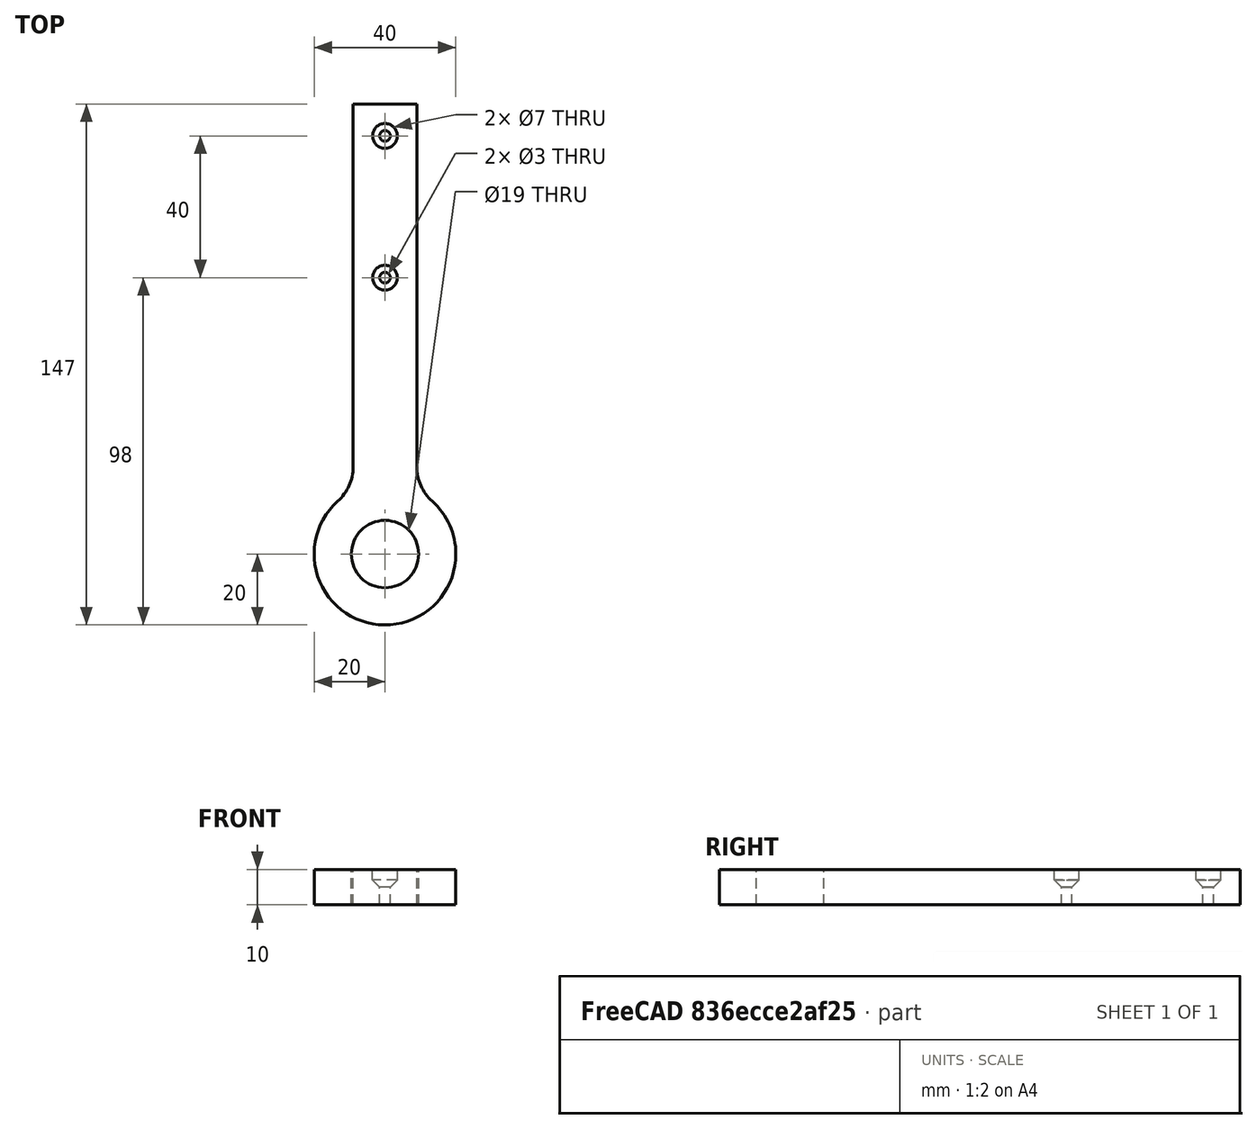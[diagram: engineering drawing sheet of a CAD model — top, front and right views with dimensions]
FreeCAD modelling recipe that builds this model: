
FCSTD DOCUMENT  (FreeCAD 0.16R6703 (Git))
Label: Asa
License: All rights reserved
LicenseURL: http://en.wikipedia.org/wiki/All_rights_reserved
objects: Part::Cylinder×4, Part::MultiFuse×4, Part::Box×1, Part::Cone×1, Part::Fillet×1, Part::Cut×1
note: 12 computed .brp shape members not serialized (recipe doc carries the construction recipe); baked Part::Feature solids carry a one-line shape summary decoded from their .brp

FEATURE [Part::Cylinder] Cylinder
  Angle = 360
  Height = 10
  Radius = 9.5
  expr: Radius = 19 / 2
FEATURE [Part::Cylinder] Cylinder001
  Angle = 360
  Height = 10
  Radius = 20
FEATURE [Part::Box] Box  label="Cube"
  Height = 10
  Length = 18
  Placement = pos=(-9,17,0) rot=(0,0,1;0rad)
  Width = 110
FEATURE [Part::Cylinder] Cylinder002
  Angle = 360
  Height = 10
  Placement = pos=(15,-5,0) rot=(0,0,1;0rad)
  Radius = 1.5
FEATURE [Part::Cylinder] Cylinder003
  Angle = 360
  Height = 10
  Placement = pos=(15,-5,8) rot=(0,0,1;0rad)
  Radius = 3.5
FEATURE [Part::Cone] Cone
  Angle = 360
  Height = 2
  Placement = pos=(15,-5,6) rot=(0,0,1;0rad)
  Radius1 = 1.5
  Radius2 = 3.5
FEATURE [Part::MultiFuse] Fusion001
  Placement = pos=(-15,123,-1) rot=(0,0,1;0rad)
  Shapes = -> [Cylinder002,Cylinder003,Cone]
FEATURE [Part::MultiFuse] Fusion002
  Placement = pos=(-15,83,-1) rot=(0,0,1;0rad)
  Shapes = -> [Cylinder002,Cylinder003,Cone]
FEATURE [Part::MultiFuse] Fusion
  Shapes = -> [Box,Cylinder001]
FEATURE [Part::Fillet] Fillet
  Base = -> Fusion
  Edges = 2 edges r=13: [Edge7,Edge10]
FEATURE [Part::MultiFuse] Fusion003
  Shapes = -> [Cylinder,Fusion001,Fusion002]
FEATURE [Part::Cut] Cut
  Base = -> Fillet
  Tool = -> Fusion003
